# Revit family: Reece_Cistern Buttons_Hideaway_Plus_Cistern Button and Plate_Remote Access_Round Button
name_source: partatom
category: Plumbing Fixtures
revit_build: Autodesk Revit 2018 (Build: 20180329_1100(x64)
units: mm (PartAtom-declared; Revit-internal decimal feet)

## family parameters
Cut with Voids When Loaded = No
Host = Face
Part Type = Normal
Room Calculation Point = Yes
Round Connector Dimension = Use Diameter
Shared = Yes

## types (1)
- Brushed Stainless Steel
    CW Connection = No
    CWFU = 0
    Default Elevation = 1000 mm  [stored 3.28084 ft]
    Description = Hideaway+ Round Remote Access Button/ Plate Inwall Brushed Stainless Steel
    Disclaimer = THIS FILE IS THE PROPERTY OF THE REECE GROUP. IT MAY NOT BE REPRODUCED, REVERSE-ENGINEERED OR MODIFIED. ANY REPUBLICATION, TRANSMISSION OR DISTRIBUTION FOR THE PURPOSE OF COMMERCIALLY EXPLOITING THE FILES IS PROHIBITED.
    HW Connection = No
    HWFU = 0
    Keynote = Product #9503691, Reece_Cistern Buttons_Hideaway_Plus_Cistern Button and Plate_Remote Access_Round Button - Brushed Stainless Steel
    Manufacturer = Hideaway
    Model = Plus
    Reece_Detail_Additional = Remote Access
    Reece_Detail_Disclaimer = THIS FILE IS THE PROPERTY OF THE REECE GROUP. IT MAY NOT BE REPRODUCED, REVERSE-ENGINEERED OR MODIFIED. ANY REPUBLICATION, TRANSMISSION OR DISTRIBUTION FOR THE PURPOSE OF COMMERCIALLY EXPLOITING THE FILES IS PROHIBITED.
    Reece_Detail_Shape = Round Button
    Reece_Material_Main = Reece_Brass_Brushed Stainless Steel
    Reece_Material_Secondary = Reece_Brass_Brushed Stainless Steel
    Reece_Overall_Height = 108 mm
    Reece_Overall_Width = 175 mm  [stored 0.574147 ft]
    Reece_Plate_Thickness = 4 mm  [stored 0.0131234 ft]
    Reece_Product_Brand = Hideaway
    Reece_Product_Description = Hideaway+ Round Remote Access Button/ Plate Inwall Brushed Stainless Steel
    Reece_Product_Mount = Wall Mounted
    Reece_Product_Number = 9503691
    Reece_Product_Sub Brand = Plus
    Reece_Product_Type = Cistern Buttons
    Reece_Product_Web Page = https://www.reece.com.au
    Type Comments = Cistern Buttons
    URL = https://www.reece.com.au
    Vent Connection = No
    WFU = 0
    Waste Connection = No

note: [stored X ft] marks values corroborated as IEEE doubles in the binary element streams (Revit-internal decimal feet)

## geometry (parser evidence)
native form markers: Sweep x3
no freeform markers — native parametric forms only
